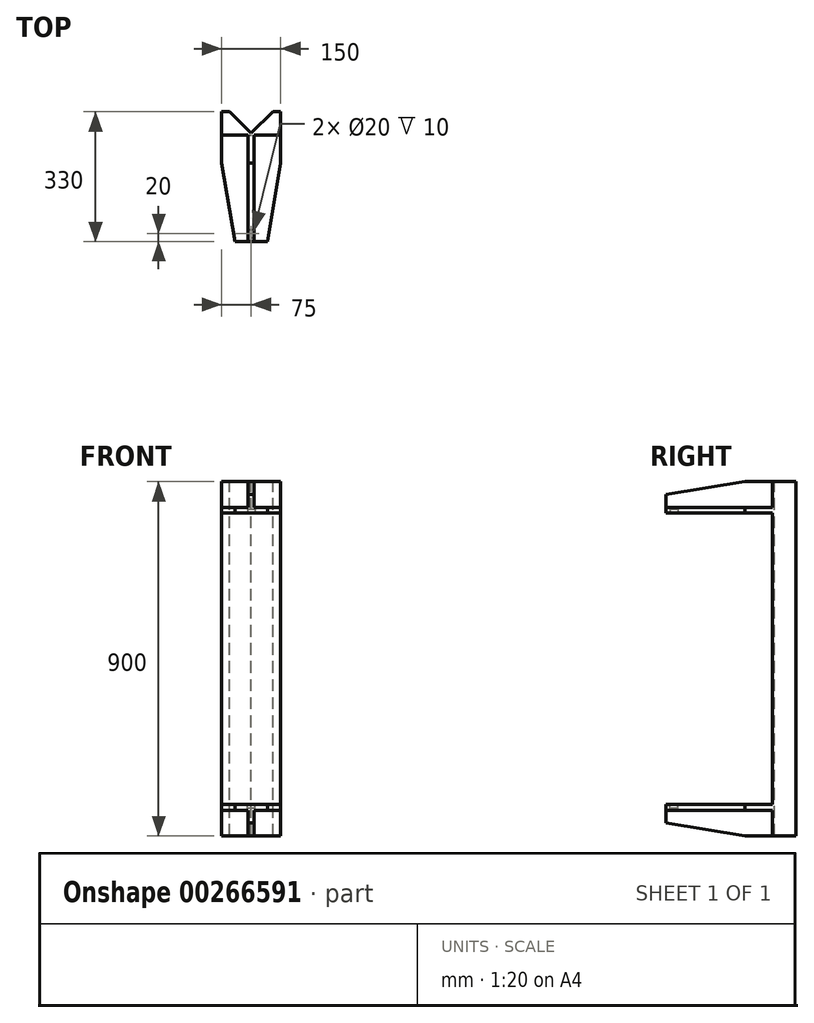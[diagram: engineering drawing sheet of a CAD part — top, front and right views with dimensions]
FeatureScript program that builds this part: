
annotation { "Feature Type Name" : "Feature", "Feature Type Description" : "" }
export const myFeature = defineFeature(function(context is Context, id is Id, definition is map)
    precondition{}
    {
        {
            var Q0;
            Q0=qCreatedBy(makeId("Front.planeOp"),FACE);
            var sketch = newSketch(context, id + "F0", { "sketchPlane" : qUnion([Q0])});
            skLineSegment(sketch, "E0.bottom", {"start": v(0, 0) * mm, "end": v(150, 0) * mm});
            skLineSegment(sketch, "E0.top", {"start": v(0, -900) * mm, "end": v(150, -900) * mm});
            skLineSegment(sketch, "E0.left", {"start": v(0, 0) * mm, "end": v(0, -900) * mm});
            skLineSegment(sketch, "E0.right", {"start": v(150, 0) * mm, "end": v(150, -900) * mm});
            skSolve(sketch);
        }
        {
            var Q0;
            Q0 = qSketchRegion(id + "F0", true);
            extrude(context, id + "F1", {"entities" : qUnion([Q0]), "depth" : 80 * mm, "offsetDistance" : 25 * mm});
        }
        {
            var Q0;
            Q0=makeQuery(id+"F1.opExtrude","CAP_FACE",FACE,{"disambiguationData":[OSD([sQuery(id+"F0.wireOp",EDGE,"E0.bottom"),sQuery(id+"F0.wireOp",EDGE,"E0.top"),sQuery(id+"F0.wireOp",EDGE,"E0.left"),sQuery(id+"F0.wireOp",EDGE,"E0.right")])],"isStart":false});
            var sketch = newSketch(context, id + "F2", { "sketchPlane" : qUnion([Q0])});
            skLineSegment(sketch, "E1.bottom", {"start": v(0, -65) * mm, "end": v(150, -65) * mm});
            skLineSegment(sketch, "E1.top", {"start": v(0, -80) * mm, "end": v(150, -80) * mm});
            skLineSegment(sketch, "E1.left", {"start": v(0, -65) * mm, "end": v(0, -80) * mm});
            skLineSegment(sketch, "E1.right", {"start": v(150, -65) * mm, "end": v(150, -80) * mm});
            skLineSegment(sketch, "E2.bottom", {"start": v(67.5, 0) * mm, "end": v(82.5, 0) * mm});
            skLineSegment(sketch, "E2.top", {"start": v(67.5, -65) * mm, "end": v(82.5, -65) * mm});
            skLineSegment(sketch, "E2.left", {"start": v(67.5, 0) * mm, "end": v(67.5, -65) * mm});
            skLineSegment(sketch, "E2.right", {"start": v(82.5, 0) * mm, "end": v(82.5, -65) * mm});
            skLineSegment(sketch, "E3", {"start": v(150, -450) * mm, "end": v(210.22, -450) * mm});
            skLineSegment(sketch, "E4.MirrorCS", {"start": v(67.5, -835) * mm, "end": v(82.5, -835) * mm});
            skLineSegment(sketch, "E5.MirrorCS", {"start": v(67.5, -900) * mm, "end": v(82.5, -900) * mm});
            skLineSegment(sketch, "E6.MirrorCS", {"start": v(150, -835) * mm, "end": v(150, -820) * mm});
            skLineSegment(sketch, "E7.MirrorCS", {"start": v(0, -835) * mm, "end": v(0, -820) * mm});
            skLineSegment(sketch, "E8.MirrorCS", {"start": v(67.5, -900) * mm, "end": v(67.5, -835) * mm});
            skLineSegment(sketch, "E9.MirrorCS", {"start": v(0, -820) * mm, "end": v(150, -820) * mm});
            skLineSegment(sketch, "E10.MirrorCS", {"start": v(82.5, -900) * mm, "end": v(82.5, -835) * mm});
            skLineSegment(sketch, "E11.MirrorCS", {"start": v(0, -835) * mm, "end": v(150, -835) * mm});
            skSolve(sketch);
        }
        {
            var Q0;
            Q0=makeQuery(id+"F2.imprint","IMPRINT",FACE,{"disambiguationData":[TD([[makeQuery(id+"F2.imprint","IMPRINT",EDGE,{"derivedFrom":sQuery(id+"F2.wireOp",EDGE,"E1.top")}),1.0]])]});
            var Q1;
            Q1=makeQuery(id+"F2.imprint","IMPRINT",FACE,{"disambiguationData":[TD([[makeQuery(id+"F2.imprint","IMPRINT",EDGE,{"derivedFrom":sQuery(id+"F2.wireOp",EDGE,"E2.bottom")}),-1.0]])]});
            var Q2;
            {var subQ3=sQuery(id+"F2.wireOp",EDGE,"E6.MirrorCS");Q2=makeQuery(id+"F2.imprint","IMPRINT",FACE,{"disambiguationData":[TD([[makeQuery(id+"F2.imprint","IMPRINT",EDGE,{"derivedFrom":subQ3}),-1.0]])]});}
            var Q3;
            Q3=makeQuery(id+"F2.imprint","IMPRINT",FACE,{"disambiguationData":[TD([[makeQuery(id+"F2.imprint","IMPRINT",EDGE,{"derivedFrom":sQuery(id+"F2.wireOp",EDGE,"E5.MirrorCS")}),1.0]])]});
            extrude(context, id + "F3", {"entities" : qUnion([Q0, Q1, Q2, Q3]), "operationType" : NewBodyOperationType.ADD, "depth" : 270 * mm});
        }
        {
            var Q0;
            Q0=makeQuery(id+"F3.opExtrude","SWEPT_FACE",FACE,{"disambiguationData":[OSD([sQuery(id+"F2.wireOp",EDGE,"E2.left")])]});
            var sketch = newSketch(context, id + "F4", { "sketchPlane" : qUnion([Q0])});
            skLineSegment(sketch, "E12", {"start": v(150, 0) * mm, "end": v(350, -32.5) * mm});
            skSolve(sketch);
        }
        {
            var Q0;
            {var subQ0=sQuery(id+"F4.wireOp",EDGE,"E12");Q0=makeQuery(id+"F4.imprint","IMPRINT",FACE,{"disambiguationData":[TD([[makeQuery(id+"F4.imprint","IMPRINT",EDGE,{"derivedFrom":subQ0}),1.0]])]});}
            extrude(context, id + "F5", {"entities" : qUnion([Q0]), "operationType" : NewBodyOperationType.REMOVE, "oppositeDirection" : true, "depth" : 25 * mm});
        }
        {
            var Q0;
            {var subQ0=sQuery(id+"F2.wireOp",EDGE,"E1.bottom");Q0=makeQuery(id+"F3.opExtrude","SWEPT_FACE",FACE,{"disambiguationData":[OSD([subQ0]),TDD([makeQuery(id+"F2.imprint","IMPRINT",EDGE,{"disambiguationData":[TD([[makeQuery(id+"F2.imprint","INTERSECT",VERTEX,{"derivedFrom":[makeQuery(id+"F1.opExtrude","CAP_EDGE",EDGE,{"disambiguationData":[OSD([sQuery(id+"F0.wireOp",EDGE,"E0.right")])],"isStart":false}),subQ0,sQuery(id+"F2.wireOp",EDGE,"E1.right")]}),1.0]])],"derivedFrom":subQ0})])]});}
            var sketch = newSketch(context, id + "F6", { "sketchPlane" : qUnion([Q0])});
            skLineSegment(sketch, "E13", {"start": v(116.25, -350) * mm, "end": v(150, -150) * mm});
            skLineSegment(sketch, "E14", {"start": v(150, -150) * mm, "end": v(150, -350) * mm});
            skLineSegment(sketch, "E15", {"start": v(150, -350) * mm, "end": v(116.25, -350) * mm});
            skSolve(sketch);
        }
        {
            var Q0;
            Q0 = qSketchRegion(id + "F6", true);
            extrude(context, id + "F7", {"entities" : qUnion([Q0]), "operationType" : NewBodyOperationType.REMOVE, "oppositeDirection" : true, "depth" : 25 * mm});
        }
        {
            var Q0;
            {var subQ0=sQuery(id+"F2.wireOp",EDGE,"E1.bottom");Q0=makeQuery(id+"F3.opExtrude","SWEPT_FACE",FACE,{"disambiguationData":[OSD([subQ0]),TDD([makeQuery(id+"F2.imprint","IMPRINT",EDGE,{"disambiguationData":[TD([[makeQuery(id+"F2.imprint","INTERSECT",VERTEX,{"derivedFrom":[makeQuery(id+"F1.opExtrude","CAP_EDGE",EDGE,{"disambiguationData":[OSD([sQuery(id+"F0.wireOp",EDGE,"E0.left")])],"isStart":false}),subQ0,sQuery(id+"F2.wireOp",EDGE,"E1.left")]}),-1.0]])],"derivedFrom":subQ0})])]});}
            var sketch = newSketch(context, id + "F8", { "sketchPlane" : qUnion([Q0])});
            skLineSegment(sketch, "E16", {"start": v(33.75, -350) * mm, "end": v(0, -150) * mm});
            skLineSegment(sketch, "E17", {"start": v(0, -150) * mm, "end": v(0, -350) * mm});
            skLineSegment(sketch, "E18", {"start": v(0, -350) * mm, "end": v(33.75, -350) * mm});
            skSolve(sketch);
        }
        {
            var Q0;
            Q0 = qSketchRegion(id + "F8", true);
            extrude(context, id + "F9", {"entities" : qUnion([Q0]), "operationType" : NewBodyOperationType.REMOVE, "oppositeDirection" : true, "depth" : 25 * mm});
        }
        {
            var Q0;
            {var subQ0=sQuery(id+"F2.wireOp",EDGE,"E11.MirrorCS");Q0=makeQuery(id+"F3.opExtrude","SWEPT_FACE",FACE,{"disambiguationData":[OSD([subQ0]),TDD([makeQuery(id+"F2.imprint","IMPRINT",EDGE,{"disambiguationData":[TD([[makeQuery(id+"F2.imprint","INTERSECT",VERTEX,{"derivedFrom":[sQuery(id+"F2.wireOp",EDGE,"E10.MirrorCS"),subQ0]}),-1.0]])],"derivedFrom":subQ0})])]});}
            var sketch = newSketch(context, id + "F10", { "sketchPlane" : qUnion([Q0])});
            skLineSegment(sketch, "E19", {"start": v(116.25, 350) * mm, "end": v(150, 150) * mm});
            skLineSegment(sketch, "E20", {"start": v(150, 150) * mm, "end": v(150, 350) * mm});
            skLineSegment(sketch, "E21", {"start": v(150, 350) * mm, "end": v(116.25, 350) * mm});
            skSolve(sketch);
        }
        {
            var Q0;
            Q0 = qSketchRegion(id + "F10", true);
            extrude(context, id + "F11", {"entities" : qUnion([Q0]), "operationType" : NewBodyOperationType.REMOVE, "oppositeDirection" : true, "depth" : 25 * mm});
        }
        {
            var Q0;
            {var subQ0=sQuery(id+"F2.wireOp",EDGE,"E11.MirrorCS");Q0=makeQuery(id+"F3.opExtrude","SWEPT_FACE",FACE,{"disambiguationData":[OSD([subQ0]),TDD([makeQuery(id+"F2.imprint","IMPRINT",EDGE,{"disambiguationData":[TD([[makeQuery(id+"F2.imprint","INTERSECT",VERTEX,{"derivedFrom":[sQuery(id+"F2.wireOp",EDGE,"E8.MirrorCS"),subQ0]}),1.0]])],"derivedFrom":subQ0})])]});}
            var sketch = newSketch(context, id + "F12", { "sketchPlane" : qUnion([Q0])});
            skLineSegment(sketch, "E22", {"start": v(33.75, 350) * mm, "end": v(0, 150) * mm});
            skLineSegment(sketch, "E23", {"start": v(0, 150) * mm, "end": v(0, 350) * mm});
            skLineSegment(sketch, "E24", {"start": v(0, 350) * mm, "end": v(33.75, 350) * mm});
            skSolve(sketch);
        }
        {
            var Q0;
            Q0 = qSketchRegion(id + "F12", true);
            extrude(context, id + "F13", {"entities" : qUnion([Q0]), "operationType" : NewBodyOperationType.REMOVE, "oppositeDirection" : true, "depth" : 25 * mm});
        }
        {
            var Q0;
            Q0=makeQuery(id+"F3.opExtrude","SWEPT_FACE",FACE,{"disambiguationData":[OSD([sQuery(id+"F2.wireOp",EDGE,"E8.MirrorCS")])]});
            var sketch = newSketch(context, id + "F14", { "sketchPlane" : qUnion([Q0])});
            skLineSegment(sketch, "E25", {"start": v(350, -867.5) * mm, "end": v(150, -900) * mm});
            skLineSegment(sketch, "E26", {"start": v(150, -900) * mm, "end": v(350, -900) * mm});
            skLineSegment(sketch, "E27", {"start": v(350, -900) * mm, "end": v(350, -867.5) * mm});
            skSolve(sketch);
        }
        {
            var Q0;
            Q0 = qSketchRegion(id + "F14", true);
            extrude(context, id + "F15", {"entities" : qUnion([Q0]), "operationType" : NewBodyOperationType.REMOVE, "oppositeDirection" : true, "depth" : 25 * mm});
        }
        {
            var Q0;
            Q0=makeQuery(id+"F3.opExtrude","SWEPT_FACE",FACE,{"disambiguationData":[OSD([sQuery(id+"F2.wireOp",EDGE,"E1.top")])]});
            var sketch = newSketch(context, id + "F16", { "sketchPlane" : qUnion([Q0])});
            skCircle(sketch, "E28", {"center": v(75, 330) * mm, "radius": 10 * mm});
            skPoint(sketch, "E28.centerSnap0", {"position": v(75, 350) * mm});
            skSolve(sketch);
        }
        {
            var Q0;
            Q0 = qSketchRegion(id + "F16", true);
            extrude(context, id + "F17", {"entities" : qUnion([Q0]), "operationType" : NewBodyOperationType.REMOVE, "oppositeDirection" : true, "depth" : 10 * mm});
        }
        {
            var Q0;
            Q0=makeQuery(id+"F3.opExtrude","SWEPT_FACE",FACE,{"disambiguationData":[OSD([sQuery(id+"F2.wireOp",EDGE,"E9.MirrorCS")])]});
            var sketch = newSketch(context, id + "F18", { "sketchPlane" : qUnion([Q0])});
            skCircle(sketch, "E29", {"center": v(75, -330) * mm, "radius": 10 * mm});
            skPoint(sketch, "E29.centerSnap0", {"position": v(75, -350) * mm});
            skSolve(sketch);
        }
        {
            var Q0;
            Q0=makeQuery(id+"F18.imprint","IMPRINT",FACE,{"disambiguationData":[TD([[makeQuery(id+"F18.imprint","IMPRINT",EDGE,{"derivedFrom":sQuery(id+"F18.wireOp",EDGE,"E29")}),1.0]])]});
            extrude(context, id + "F19", {"entities" : qUnion([Q0]), "operationType" : NewBodyOperationType.REMOVE, "oppositeDirection" : true, "depth" : 10 * mm});
        }
        {
            var Q0;
            Q0=makeQuery(id+"F3.boolean.opBoolean","MERGE",FACE,{"derivedFrom":[makeQuery(id+"F1.opExtrude","SWEPT_FACE",FACE,{"disambiguationData":[OSD([sQuery(id+"F0.wireOp",EDGE,"E0.bottom")])]}),makeQuery(id+"F3.opExtrude","SWEPT_FACE",FACE,{"disambiguationData":[OSD([sQuery(id+"F2.wireOp",EDGE,"E2.bottom")])]})]});
            var sketch = newSketch(context, id + "F20", { "sketchPlane" : qUnion([Q0])});
            skLineSegment(sketch, "E30", {"start": v(0, 0) * mm, "end": v(75, -75) * mm});
            skLineSegment(sketch, "E31", {"start": v(75, -75) * mm, "end": v(150, 0) * mm});
            skLineSegment(sketch, "E32", {"start": v(0, -20) * mm, "end": v(150, -20) * mm});
            skSolve(sketch);
        }
        {
            var Q0;
            Q0 = qSketchRegion(id + "F20", true);
            var Q1;
            Q1=makeQuery(id+"F20.imprint","IMPRINT",FACE,{"disambiguationData":[TD([[makeQuery(id+"F20.imprint","IMPRINT",EDGE,{"derivedFrom":sQuery(id+"F20.wireOp",EDGE,"E30")}),1.0]])]});
            var Q2;
            {var subQ0=sQuery(id+"F20.wireOp",EDGE,"E30");var subQ4=sQuery(id+"F20.wireOp",EDGE,"E32");var subQ5=makeQuery(id+"F20.imprint","INTERSECT",VERTEX,{"derivedFrom":[subQ0,subQ4]});Q2=makeQuery(id+"F20.imprint","IMPRINT",FACE,{"disambiguationData":[TD([[makeQuery(id+"F20.imprint","IMPRINT",EDGE,{"disambiguationData":[TD([[subQ5,1.0]])],"derivedFrom":subQ4}),1.0]])]});}
            var Q3;
            {var subQ1=sQuery(id+"F0.wireOp",EDGE,"E0.bottom");var subQ2=makeQuery(id+"F1.opExtrude","CAP_EDGE",EDGE,{"disambiguationData":[OSD([subQ1])],"isStart":true});Q3=makeQuery(id+"F20.imprint","IMPRINT",FACE,{"disambiguationData":[TD([[makeQuery(id+"F20.imprint","IMPRINT",EDGE,{"derivedFrom":subQ2}),-1.0]])]});}
            var Q4;
            {var subQ0=sQuery(id+"F20.wireOp",EDGE,"E31");var subQ4=sQuery(id+"F20.wireOp",EDGE,"E32");var subQ5=makeQuery(id+"F20.imprint","INTERSECT",VERTEX,{"derivedFrom":[subQ0,subQ4]});Q4=makeQuery(id+"F20.imprint","IMPRINT",FACE,{"disambiguationData":[TD([[makeQuery(id+"F20.imprint","IMPRINT",EDGE,{"disambiguationData":[TD([[subQ5,-1.0]])],"derivedFrom":subQ4}),1.0]])]});}
            extrude(context, id + "F21", {"entities" : qUnion([Q0, Q1, Q2, Q3, Q4]), "operationType" : NewBodyOperationType.REMOVE, "endBound" : BoundingType.THROUGH_ALL, "oppositeDirection" : true, "depth" : 25 * mm, "offsetDistance" : 25 * mm});
        }
    });
